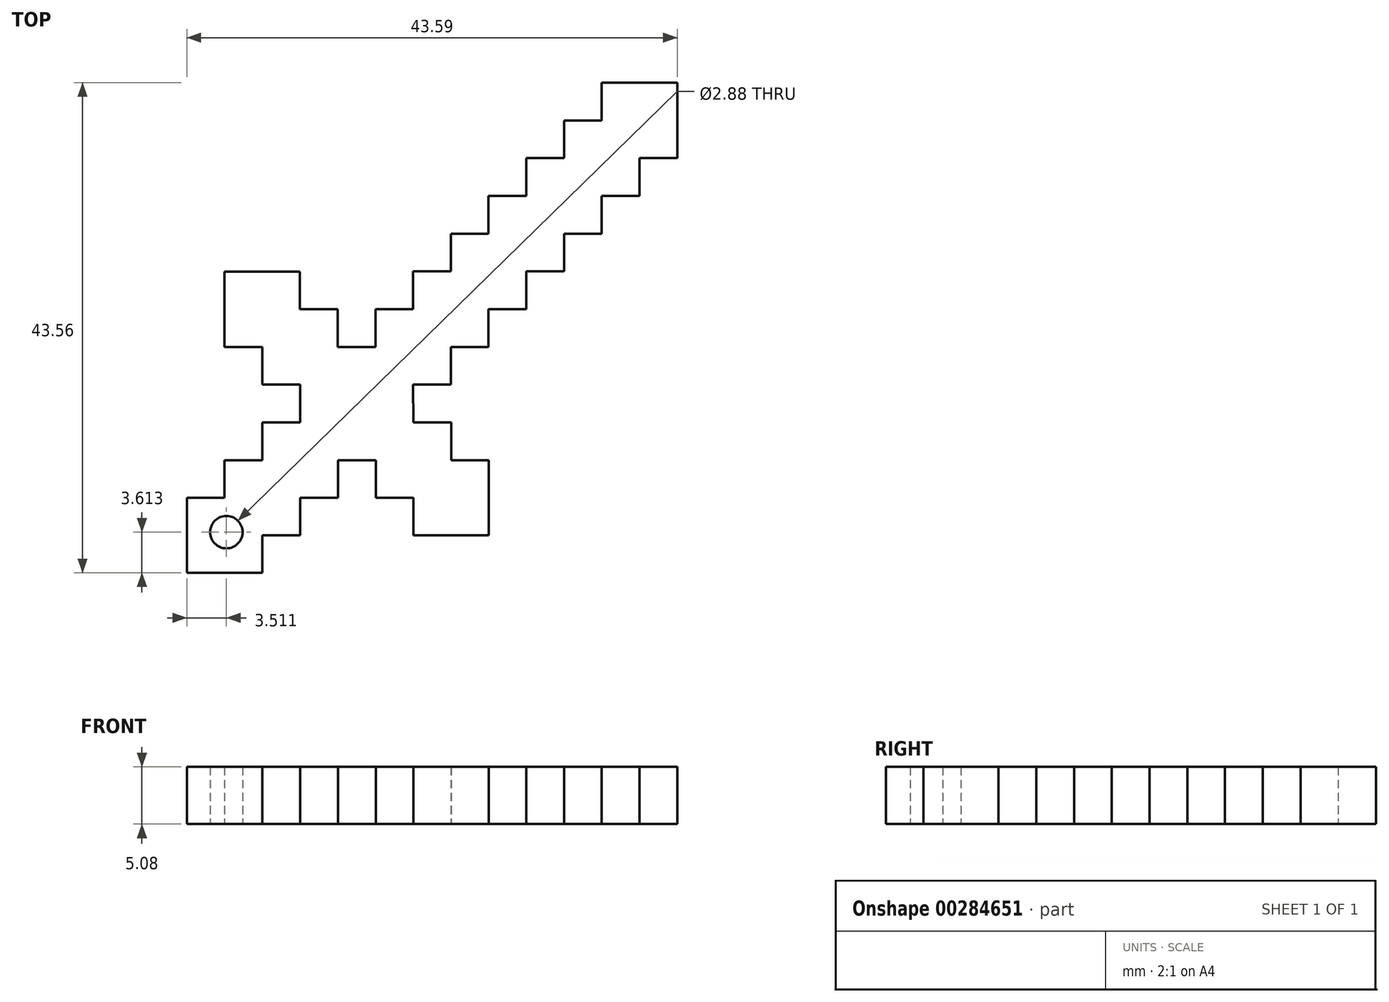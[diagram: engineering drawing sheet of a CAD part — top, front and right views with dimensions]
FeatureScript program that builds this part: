
annotation { "Feature Type Name" : "Feature", "Feature Type Description" : "" }
export const myFeature = defineFeature(function(context is Context, id is Id, definition is map)
    precondition{}
    {
        {
            var Q0;
            Q0=qCreatedBy(makeId("Top.planeOp"),FACE);
            var sketch = newSketch(context, id + "F0", { "sketchPlane" : qUnion([Q0])});
            skLineSegment(sketch, "E0", {"start": v(-11.01, -7.9) * mm, "end": v(-11.01, -4.54) * mm});
            skLineSegment(sketch, "E1", {"start": v(-11.01, -4.54) * mm, "end": v(-7.66, -4.54) * mm});
            skLineSegment(sketch, "E2", {"start": v(-7.66, -4.54) * mm, "end": v(-7.66, -1.18) * mm});
            skLineSegment(sketch, "E3", {"start": v(-7.66, -1.18) * mm, "end": v(-4.3, -1.18) * mm});
            skLineSegment(sketch, "E4", {"start": v(-4.3, -1.18) * mm, "end": v(-4.3, 2.17) * mm});
            skLineSegment(sketch, "E5", {"start": v(-4.3, 2.17) * mm, "end": v(-0.95, 2.17) * mm});
            skLineSegment(sketch, "E6", {"start": v(-0.95, 2.17) * mm, "end": v(-0.95, 5.52) * mm});
            skLineSegment(sketch, "E7", {"start": v(-0.95, 5.52) * mm, "end": v(2.4, 5.52) * mm});
            skLineSegment(sketch, "E8", {"start": v(2.4, 5.52) * mm, "end": v(2.4, 8.88) * mm});
            skLineSegment(sketch, "E9", {"start": v(2.4, 8.88) * mm, "end": v(5.75, 8.88) * mm});
            skLineSegment(sketch, "E10", {"start": v(5.75, 8.88) * mm, "end": v(5.75, 12.23) * mm});
            skLineSegment(sketch, "E11", {"start": v(5.75, 12.23) * mm, "end": v(9.1, 12.23) * mm});
            skLineSegment(sketch, "E12", {"start": v(9.1, 12.23) * mm, "end": v(9.1, 15.59) * mm});
            skLineSegment(sketch, "E13", {"start": v(9.1, 15.59) * mm, "end": v(15.82, 15.59) * mm});
            skLineSegment(sketch, "E14", {"start": v(15.82, 15.59) * mm, "end": v(15.82, 8.88) * mm});
            skLineSegment(sketch, "E15", {"start": v(15.82, 8.88) * mm, "end": v(12.46, 8.88) * mm});
            skLineSegment(sketch, "E16", {"start": v(12.46, 8.88) * mm, "end": v(12.46, 5.52) * mm});
            skLineSegment(sketch, "E17", {"start": v(12.46, 5.52) * mm, "end": v(9.1, 5.52) * mm});
            skLineSegment(sketch, "E18", {"start": v(9.1, 5.52) * mm, "end": v(9.1, 2.17) * mm});
            skLineSegment(sketch, "E19", {"start": v(9.1, 2.17) * mm, "end": v(5.75, 2.17) * mm});
            skLineSegment(sketch, "E20", {"start": v(5.75, 2.17) * mm, "end": v(5.75, -1.18) * mm});
            skLineSegment(sketch, "E21", {"start": v(5.75, -1.18) * mm, "end": v(2.4, -1.18) * mm});
            skLineSegment(sketch, "E22", {"start": v(2.4, -1.18) * mm, "end": v(2.4, -4.54) * mm});
            skLineSegment(sketch, "E23", {"start": v(2.4, -4.54) * mm, "end": v(-0.95, -4.54) * mm});
            skLineSegment(sketch, "E24", {"start": v(-0.95, -4.54) * mm, "end": v(-0.95, -7.9) * mm});
            skLineSegment(sketch, "E25", {"start": v(-0.95, -7.9) * mm, "end": v(-4.3, -7.9) * mm});
            skLineSegment(sketch, "E26", {"start": v(-4.3, -7.9) * mm, "end": v(-4.3, -11.24) * mm});
            skLineSegment(sketch, "E27", {"start": v(-4.3, -11.24) * mm, "end": v(-7.66, -11.24) * mm});
            skLineSegment(sketch, "E28", {"start": v(-11.01, -7.9) * mm, "end": v(-14.37, -7.9) * mm});
            skLineSegment(sketch, "E29", {"start": v(-14.37, -7.9) * mm, "end": v(-14.37, -4.54) * mm});
            skLineSegment(sketch, "E30", {"start": v(-14.37, -4.54) * mm, "end": v(-17.73, -4.54) * mm});
            skLineSegment(sketch, "E31", {"start": v(-17.73, -4.54) * mm, "end": v(-17.73, -1.2) * mm});
            skLineSegment(sketch, "E32", {"start": v(-17.73, -1.2) * mm, "end": v(-21.07, -1.2) * mm});
            skLineSegment(sketch, "E33", {"start": v(-21.07, -1.2) * mm, "end": v(-24.44, -1.2) * mm});
            skLineSegment(sketch, "E34", {"start": v(-24.44, -1.2) * mm, "end": v(-24.44, -7.9) * mm});
            skLineSegment(sketch, "E35", {"start": v(-24.44, -7.9) * mm, "end": v(-21.07, -7.9) * mm});
            skLineSegment(sketch, "E36", {"start": v(-21.07, -7.9) * mm, "end": v(-21.07, -11.24) * mm});
            skLineSegment(sketch, "E37", {"start": v(-21.07, -11.24) * mm, "end": v(-17.71, -11.24) * mm});
            skLineSegment(sketch, "E38", {"start": v(-17.71, -11.24) * mm, "end": v(-17.71, -14.6) * mm});
            skLineSegment(sketch, "E39", {"start": v(-17.71, -14.6) * mm, "end": v(-21.07, -14.6) * mm});
            skLineSegment(sketch, "E40", {"start": v(-21.07, -14.6) * mm, "end": v(-21.07, -17.96) * mm});
            skLineSegment(sketch, "E41", {"start": v(-21.07, -17.96) * mm, "end": v(-24.42, -17.96) * mm});
            skLineSegment(sketch, "E42", {"start": v(-24.42, -17.96) * mm, "end": v(-24.42, -21.3) * mm});
            skLineSegment(sketch, "E43", {"start": v(-24.42, -21.3) * mm, "end": v(-27.77, -21.3) * mm});
            skLineSegment(sketch, "E44", {"start": v(-27.77, -21.3) * mm, "end": v(-27.77, -27.97) * mm});
            skLineSegment(sketch, "E45", {"start": v(-27.77, -27.97) * mm, "end": v(-21.06, -27.97) * mm});
            skLineSegment(sketch, "E46", {"start": v(-21.06, -27.97) * mm, "end": v(-21.06, -24.62) * mm});
            skLineSegment(sketch, "E47", {"start": v(-21.06, -24.62) * mm, "end": v(-17.7, -24.62) * mm});
            skLineSegment(sketch, "E48", {"start": v(-17.7, -24.62) * mm, "end": v(-17.7, -21.3) * mm});
            skLineSegment(sketch, "E49", {"start": v(-17.7, -21.3) * mm, "end": v(-14.33, -21.3) * mm});
            skLineSegment(sketch, "E50", {"start": v(-14.33, -21.3) * mm, "end": v(-14.33, -17.96) * mm});
            skLineSegment(sketch, "E51", {"start": v(-14.33, -17.96) * mm, "end": v(-10.97, -17.96) * mm});
            skLineSegment(sketch, "E52", {"start": v(-10.97, -17.96) * mm, "end": v(-10.97, -21.3) * mm});
            skLineSegment(sketch, "E53", {"start": v(-10.97, -21.3) * mm, "end": v(-7.63, -21.3) * mm});
            skLineSegment(sketch, "E54", {"start": v(-7.63, -21.3) * mm, "end": v(-7.63, -24.62) * mm});
            skLineSegment(sketch, "E55", {"start": v(-7.63, -24.62) * mm, "end": v(-4.27, -24.62) * mm});
            skLineSegment(sketch, "E56", {"start": v(-4.27, -24.62) * mm, "end": v(-0.92, -24.62) * mm});
            skLineSegment(sketch, "E57", {"start": v(-0.92, -24.62) * mm, "end": v(-0.92, -17.96) * mm});
            skLineSegment(sketch, "E58", {"start": v(-0.92, -17.96) * mm, "end": v(-4.27, -17.96) * mm});
            skLineSegment(sketch, "E59", {"start": v(-4.27, -17.96) * mm, "end": v(-4.27, -14.6) * mm});
            skLineSegment(sketch, "E60", {"start": v(-4.27, -14.6) * mm, "end": v(-7.63, -14.6) * mm});
            skLineSegment(sketch, "E61", {"start": v(-7.63, -14.6) * mm, "end": v(-7.66, -11.24) * mm});
            skCircle(sketch, "E62", {"center": v(-24.26, -24.36) * mm, "radius": 1.44 * mm});
            skSolve(sketch);
        }
        {
            var Q0;
            Q0=makeQuery(id+"F0.imprint","IMPRINT",FACE,{"disambiguationData":[TD([[makeQuery(id+"F0.imprint","IMPRINT",EDGE,{"derivedFrom":sQuery(id+"F0.wireOp",EDGE,"E0")}),-1.0]])]});
            extrude(context, id + "F1", {"entities" : qUnion([Q0]), "depth" : 5.08 * mm});
        }
    });
